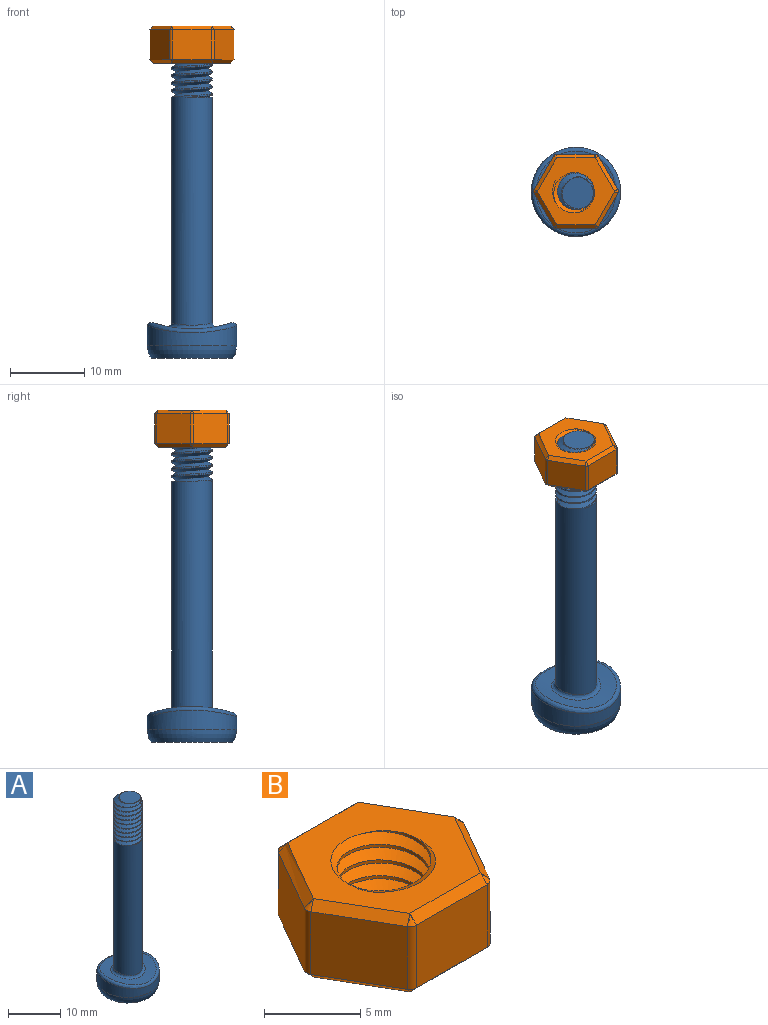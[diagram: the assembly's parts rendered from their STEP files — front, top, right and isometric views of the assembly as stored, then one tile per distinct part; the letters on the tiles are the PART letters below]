
ASSEMBLY  parts=2 mates=1
PART A: 22 faces, bbox 13.4x13.4x46 mm
  f0: cylinder r=17.25mm len=11mm, axis (0,-1,0), area 59.2mm2, adj f17,f18
  f1: cylinder r=6mm len=12mm, axis (0,0,-1), area 96.9mm2, adj f18,f21
  f2: plane 11x11mm, normal (0,0,-1), area 95mm2, adj f21
  f3: cylinder r=2.75mm len=31.6mm, axis (0,0,-1), area 529.1mm2, adj f4,f14,f15,f16,f17
  f4: cylinder r=2.75mm len=5.5mm, axis (0,0,-1), area 3.5mm2, adj f3,f5,f14,f15
  f5: cylinder r=2.75mm len=5.5mm, axis (0,0,-1), area 3.5mm2, adj f4,f6,f14,f15
  f6: cylinder r=2.75mm len=5.5mm, axis (0,0,-1), area 3.5mm2, adj f5,f7,f14,f15
  f7: cylinder r=2.75mm len=5.5mm, axis (0,0,-1), area 3.5mm2, adj f6,f8,f14,f15
  f8: cylinder r=2.75mm len=5.5mm, axis (0,0,-1), area 3.5mm2, adj f7,f9,f14,f15
  f9: cylinder r=2.75mm len=5.5mm, axis (0,0,-1), area 3.4mm2, adj f8,f10,f14,f15
  f10: cylinder r=2.75mm len=5.5mm, axis (0,0,-1), area 3.5mm2, adj f9,f11,f14,f15
  f11: cylinder r=2.75mm len=5.5mm, axis (0,0,-1), area 3.5mm2, adj f10,f12,f14,f15
  f12: cylinder r=2.75mm len=3.52mm, axis (0,0,-1), area 1mm2, adj f11,f14,f15,f19
  f13: plane 4.26x4.25mm, normal (0,0,1), area 13.5mm2, adj f19,f20
  f14: bspline ~10.07x6.35mm, area 109.9mm2, adj f3,f4,f5,f6,f7,f8,f9,f10
  f15: bspline ~10.62x6.35mm, area 115.3mm2, adj f3,f4,f5,f6,f7,f8,f9,f10
  f16: plane 5.94x5.94mm, normal (0,0,1), area 4.4mm2, adj f3,f14,f15
  f17: bspline ~6.69x6.51mm, area 15.5mm2, adj f0,f3
  f18: bspline ~12.02x12.01mm, area 31.6mm2, adj f0,f1
  f19: bspline ~4.97x4.15mm, area 2.9mm2, adj f12,f13,f14,f15,f20
  f20: bspline ~4.42x3.82mm, area 0.8mm2, adj f13,f15,f19
  f21: torus R=3mm, axis (0,0,-1), area 64.4mm2, adj f1,f2
PART B: 43 faces, bbox 11.9x10.5x6.5 mm
  f0: cylinder r=2.45mm len=5mm, axis (0,0,-1), area 15.6mm2, adj f1,f40,f41,f42
  f1: plane 10.85x9.46mm, normal (0,0,-1), area 46.6mm2, adj f0,f2,f34,f35,f37,f38,f39,f40
  f2: plane 5.2x0.5mm, normal (0,-0.71,-0.71), area 3.7mm2, adj f1,f3,f32,f33
  f3: cone r=0.5mm half-angle=45deg, axis (0,0,1), area 0.2mm2, adj f2,f4,f39
  f4: cylinder r=0.5mm len=4mm, axis (0,0,-1), area 2.1mm2, adj f3,f5,f31,f32
  f5: cone r=0.5mm half-angle=45deg, axis (0,0,-1), area 0.2mm2, adj f4,f6,f30
  f6: plane 4.75x3.03mm, normal (-0.61,-0.35,0.71), area 3.7mm2, adj f5,f7,f31,f41
  f7: cone r=0.5mm half-angle=45deg, axis (0,0,-1), area 0.2mm2, adj f6,f8,f28
  f8: plane 4.75x3.03mm, normal (-0.61,0.35,0.71), area 3.7mm2, adj f7,f9,f26,f27,f41
  f9: plane 4.5x4mm, normal (-0.87,0.5,0), area 20.8mm2, adj f8,f10,f28,f38
  f10: cylinder r=0.5mm len=4mm, axis (0,0,-1), area 2.1mm2, adj f9,f11,f12,f27
  f11: cone r=0.5mm half-angle=45deg, axis (0,0,1), area 0.3mm2, adj f10,f37,f38
  f12: plane 5.2x4mm, normal (0,1,0), area 20.8mm2, adj f10,f13,f25,f37
  f13: cylinder r=0.5mm len=4mm, axis (0,0,-1), area 2.1mm2, adj f12,f14,f15,f24
  f14: cone r=0.5mm half-angle=45deg, axis (0,0,1), area 0.1mm2, adj f13,f35,f37
  f15: plane 4.5x4mm, normal (0.87,0.5,0), area 20.8mm2, adj f13,f16,f23,f35
  f16: cylinder r=0.5mm len=4mm, axis (0,0,-1), area 2.1mm2, adj f15,f17,f18,f22
  f17: cone r=0.5mm half-angle=45deg, axis (0,0,1), area 0.2mm2, adj f16,f34,f35
  f18: plane 4.5x4mm, normal (0.87,-0.5,0), area 20.8mm2, adj f16,f19,f21,f34
  f19: cylinder r=0.5mm len=4mm, axis (0,0,-1), area 2.1mm2, adj f18,f20,f32,f33
  f20: cone r=0.5mm half-angle=45deg, axis (0,0,-1), area 0.2mm2, adj f19,f21,f30
  f21: plane 5.01x3.29mm, normal (0.61,-0.35,0.71), area 3.7mm2, adj f18,f20,f22,f41
  f22: cone r=0.5mm half-angle=45deg, axis (0,0,-1), area 0.3mm2, adj f16,f21,f23
  f23: plane 5.01x3.29mm, normal (0.61,0.35,0.71), area 3.7mm2, adj f15,f22,f24,f41
  f24: cone r=0.5mm half-angle=45deg, axis (0,0,-1), area 0.3mm2, adj f13,f23,f25
  f25: plane 5.58x0.88mm, normal (0,0.71,0.71), area 3.7mm2, adj f12,f24,f26,f27,f41
  f26: cone r=0.5mm half-angle=45deg, axis (0,0,-1), area 0mm2, adj f8,f25
  f27: cone r=0.5mm half-angle=45deg, axis (0,0,-1), area 0.1mm2, adj f8,f10,f25
  f28: cylinder r=0.5mm len=4mm, axis (0,0,-1), area 2.1mm2, adj f7,f9,f29,f31
  f29: cone r=0.5mm half-angle=45deg, axis (0,0,1), area 0.1mm2, adj f28,f38,f39
  f30: plane 5.2x0.5mm, normal (0,-0.71,0.71), area 3.7mm2, adj f5,f20,f32,f41
  f31: plane 4.5x4mm, normal (-0.87,-0.5,0), area 20.8mm2, adj f4,f6,f28,f39
  f32: plane 5.2x4mm, normal (0,-1,0), area 20.8mm2, adj f2,f4,f19,f30
  f33: cone r=0.5mm half-angle=45deg, axis (0,0,1), area 0.2mm2, adj f2,f19,f34
  f34: plane 4.75x3.03mm, normal (0.61,-0.35,-0.71), area 3.7mm2, adj f1,f17,f18,f33
  f35: plane 4.75x3.03mm, normal (0.61,0.35,-0.71), area 3.7mm2, adj f1,f14,f15,f17,f36
  f36: cone r=0.5mm half-angle=45deg, axis (0,0,1), area 0mm2, adj f35,f37
  f37: plane 5.58x0.88mm, normal (0,0.71,-0.71), area 3.7mm2, adj f1,f11,f12,f14,f36
  f38: plane 5.01x3.29mm, normal (-0.61,0.35,-0.71), area 3.7mm2, adj f1,f9,f11,f29
  f39: plane 5.25x3.53mm, normal (-0.61,-0.35,-0.71), area 3.7mm2, adj f1,f3,f29,f31
  f40: bspline ~7.26x6.29mm, area 70.4mm2, adj f0,f1,f41,f42
  f41: plane 10.85x9.46mm, normal (0,0,1), area 46.6mm2, adj f0,f6,f8,f21,f23,f25,f30,f40
  f42: bspline ~7.26x6.29mm, area 70.4mm2, adj f0,f1,f40,f41
PLACE A t=(-33.84,10.21,-3.65)mm
PLACE B t=(-33.84,10.21,34.93)mm
MATE slider B.f0 <-> A.f1  axis (0,0,-1) through (-33.84,10.21,35.93)mm
